# Revit family: Shower_Head-GROHE-26569_Series
name_source: partatom
category: Plumbing Fixtures
revit_build: Autodesk Revit 2018 (Build: 20170223_1515(x64)
units: mm (PartAtom-declared; Revit-internal decimal feet)

## family parameters
Always vertical = No
Cut with Voids When Loaded = No
OmniClass Number = 23.45.05.14.17
OmniClass Title = Showers
Part Type = Normal
Room Calculation Point = No
Round Connector Dimension = Use Diameter
Shared = Yes
Work Plane-Based = Yes

## types (5) — shared parameters
Assembly Code = D2010710
CW Connection = Yes
CWFU = 3
Default Elevation = 0"
Description = 3" Ceiling Mount Shower Arm
HW Connection = Yes
HWFU = 3
Height = 7 3/4"
Installation Type = Ceiling Mounted
Length = 12 3/16"
Manufacturer = American Standard
Price = Prices may vary. Please consult Manufacturer Representative for most up-to-date price list.
Product Documentation Link = https://americanstandard.box.com
Product Page URL = https://www.grohe.us
Revised Date = 05/03/2021
URL = https://www.americanstandard-us.com
Vent Connection = No
WFU = 4
Warranty Information = One Year General Product Warranty
Waste Connection = No
Water Connection Diameter = 1/2"
Water Connection Radius = 1/4"
Width = 12 3/16"

## per-type parameters (varying)
| type | Finish | Material | Showerhead Specification |
| 26569GN0 | Metal-Grohe-GN0-Brushed Cool Sunrise | Metal-Grohe-GN0-Brushed Cool Sunrise | Grohe 26569GN0 Rainshower™ Mono 310 Shower Head - 1 Spray. GROHE StarLight. GROHE DreamSpray®. 12" Face, Recommended Rainshower™ arm: (28 540). 1.75gpm Brushed cool sunrise |
| 26569EN0 | Metal-Grohe-EN0-Brushed Nickel Infinity Finish | Metal-Grohe-EN0-Brushed Nickel Infinity Finish | Grohe 26569GN0 Rainshower™ Mono 310 Shower Head - 1 Spray. GROHE StarLight. GROHE DreamSpray®. 12" Face, Recommended Rainshower™ arm: (28 540). 1.75gpm Brushed Nickel Infinity Finish |
| 26569000 | Metal-Grohe-000-Starlight  Chrome | Metal-Grohe-000-Starlight  Chrome | Grohe 26569GN0 Rainshower™ Mono 310 Shower Head - 1 Spray. GROHE StarLight. GROHE DreamSpray®. 12" Face, Recommended Rainshower™ arm: (28 540). 1.75gpm Chrome |
| 26569A00 | Metal-Grohe-A00-Hard Graphite | Metal-Grohe-A00-Hard Graphite | Grohe 26569GN0 Rainshower™ Mono 310 Shower Head - 1 Spray. GROHE StarLight. GROHE DreamSpray®. 12" Face, Recommended Rainshower™ arm: (28 540). 1.75gpm Hard Graphite |
| 26569BE0 | Metal-Grohe-BE0-Brushed Nickel Infinity Finish | Metal-Grohe-BE0-Brushed Nickel Infinity Finish | Grohe 26569GN0 Rainshower™ Mono 310 Shower Head - 1 Spray. GROHE StarLight. GROHE DreamSpray®. 12" Face, Recommended Rainshower™ arm: (28 540). 1.75gpm Brushed Nickel |

note: column(s) folded — value = type name in every type: Model

## geometry (parser evidence)
native form markers: Sweep x2
no freeform markers — native parametric forms only
